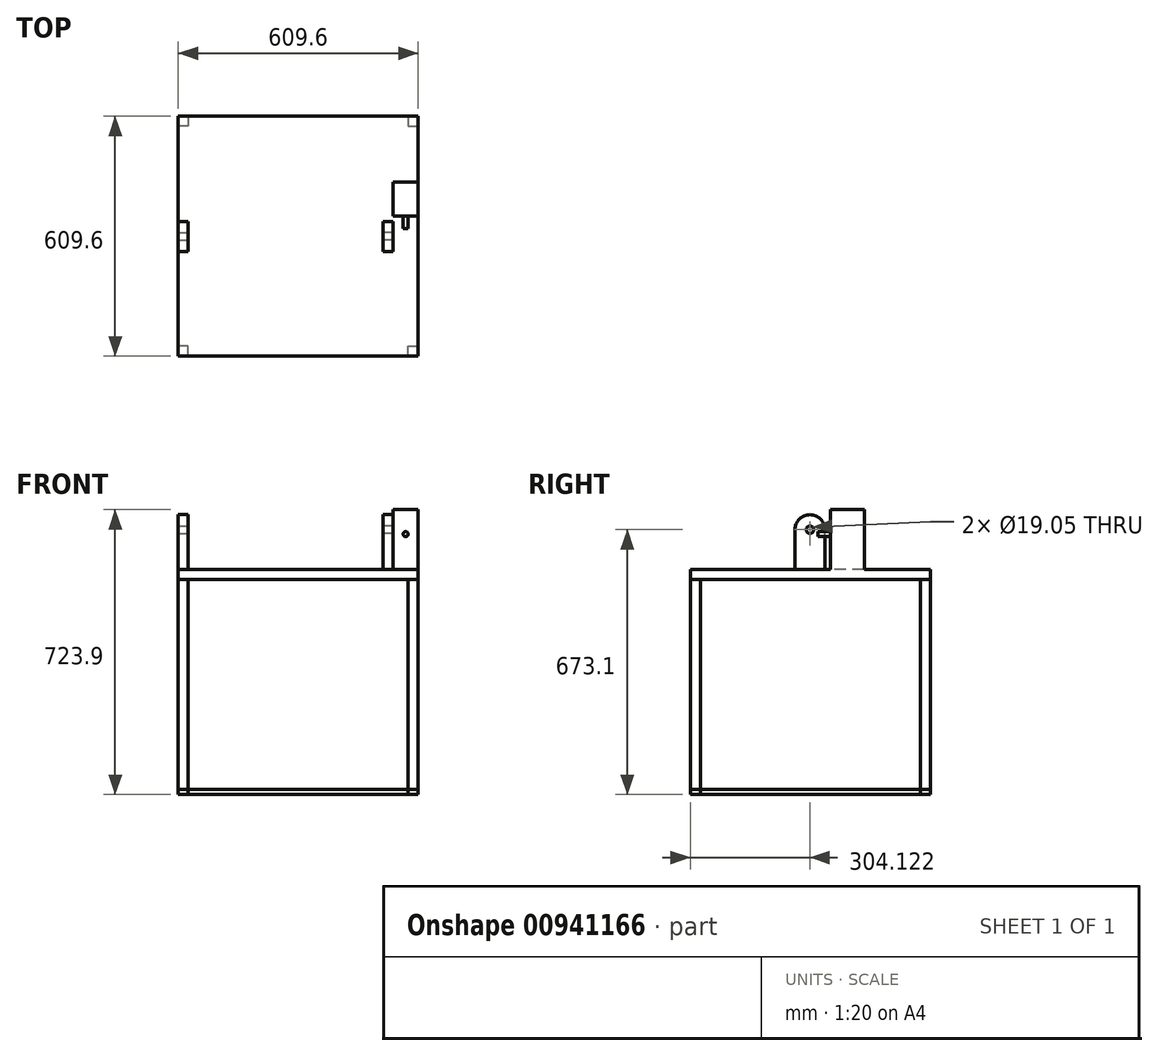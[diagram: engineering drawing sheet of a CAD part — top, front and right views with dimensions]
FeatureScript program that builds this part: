
annotation { "Feature Type Name" : "Feature", "Feature Type Description" : "" }
export const myFeature = defineFeature(function(context is Context, id is Id, definition is map)
    precondition{}
    {
        {
            var Q0;
            Q0=qCreatedBy(makeId("Top.planeOp"),FACE);
            var sketch = newSketch(context, id + "F0", { "sketchPlane" : qUnion([Q0])});
            skLineSegment(sketch, "E0.bottom", {"start": v(-279.4, -304.8) * mm, "end": v(-304.8, -304.8) * mm});
            skLineSegment(sketch, "E0.top", {"start": v(-279.4, -279.4) * mm, "end": v(-304.8, -279.4) * mm});
            skLineSegment(sketch, "E0.left", {"start": v(-279.4, -304.8) * mm, "end": v(-279.4, -279.4) * mm});
            skLineSegment(sketch, "E0.right", {"start": v(-304.8, -304.8) * mm, "end": v(-304.8, -279.4) * mm});
            skPoint(sketch, "E0.middle", {"position": v(-292.1, -292.1) * mm});
            skLineSegment(sketch, "E1.MirrorCS", {"start": v(-279.4, 304.8) * mm, "end": v(-304.8, 304.8) * mm});
            skLineSegment(sketch, "E2.MirrorCS", {"start": v(-279.4, 279.4) * mm, "end": v(-304.8, 279.4) * mm});
            skLineSegment(sketch, "E3.MirrorCS", {"start": v(-304.8, 304.8) * mm, "end": v(-304.8, 279.4) * mm});
            skLineSegment(sketch, "E4.MirrorCS", {"start": v(-279.4, 304.8) * mm, "end": v(-279.4, 279.4) * mm});
            skPoint(sketch, "E5.MirrorP", {"position": v(-292.1, 292.1) * mm});
            skLineSegment(sketch, "E6.MirrorCS", {"start": v(304.8, 304.8) * mm, "end": v(304.8, 279.4) * mm});
            skLineSegment(sketch, "E7.MirrorCS", {"start": v(279.4, 304.8) * mm, "end": v(304.8, 304.8) * mm});
            skLineSegment(sketch, "E8.MirrorCS", {"start": v(279.4, 304.8) * mm, "end": v(279.4, 279.4) * mm});
            skLineSegment(sketch, "E9.MirrorCS", {"start": v(279.4, 279.4) * mm, "end": v(304.8, 279.4) * mm});
            skLineSegment(sketch, "E10.MirrorCS", {"start": v(279.4, -304.8) * mm, "end": v(304.8, -304.8) * mm});
            skLineSegment(sketch, "E11.MirrorCS", {"start": v(279.4, -279.4) * mm, "end": v(304.8, -279.4) * mm});
            skLineSegment(sketch, "E12.MirrorCS", {"start": v(304.8, -304.8) * mm, "end": v(304.8, -279.4) * mm});
            skLineSegment(sketch, "E13.MirrorCS", {"start": v(279.4, -304.8) * mm, "end": v(279.4, -279.4) * mm});
            skPoint(sketch, "E14.MirrorP", {"position": v(292.1, 292.1) * mm});
            skPoint(sketch, "E15.MirrorP", {"position": v(292.1, -292.1) * mm});
            skLineSegment(sketch, "E16.bottom", {"start": v(-215.9, -241.3) * mm, "end": v(-241.3, -241.3) * mm});
            skLineSegment(sketch, "E16.top", {"start": v(-215.9, -215.9) * mm, "end": v(-241.3, -215.9) * mm});
            skLineSegment(sketch, "E16.left", {"start": v(-215.9, -241.3) * mm, "end": v(-215.9, -215.9) * mm});
            skLineSegment(sketch, "E16.right", {"start": v(-241.3, -241.3) * mm, "end": v(-241.3, -215.9) * mm});
            skPoint(sketch, "E16.middle", {"position": v(-228.6, -228.6) * mm});
            skPoint(sketch, "E17.1.0", {"position": v(-228.6, 228.6) * mm});
            skLineSegment(sketch, "E17.1.1", {"start": v(-241.3, 215.9) * mm, "end": v(-241.3, 241.3) * mm});
            skLineSegment(sketch, "E17.1.2", {"start": v(-215.9, 215.9) * mm, "end": v(-215.9, 241.3) * mm});
            skLineSegment(sketch, "E17.1.3", {"start": v(-241.3, 215.9) * mm, "end": v(-215.9, 215.9) * mm});
            skLineSegment(sketch, "E17.1.4", {"start": v(-241.3, 241.3) * mm, "end": v(-215.9, 241.3) * mm});
            skPoint(sketch, "E17.2.0", {"position": v(228.6, 228.6) * mm});
            skLineSegment(sketch, "E17.2.1", {"start": v(215.9, 241.3) * mm, "end": v(241.3, 241.3) * mm});
            skLineSegment(sketch, "E17.2.2", {"start": v(215.9, 215.9) * mm, "end": v(241.3, 215.9) * mm});
            skLineSegment(sketch, "E17.2.3", {"start": v(215.9, 241.3) * mm, "end": v(215.9, 215.9) * mm});
            skLineSegment(sketch, "E17.2.4", {"start": v(241.3, 241.3) * mm, "end": v(241.3, 215.9) * mm});
            skPoint(sketch, "E17.center", {"position": v(0, 0) * mm});
            skLineSegment(sketch, "E17.anchor1", {"start": v(0, 0) * mm, "end": v(-241.3, -241.3) * mm, "construction": true});
            skLineSegment(sketch, "E17.anchor2", {"start": v(0, 0) * mm, "end": v(241.3, -241.3) * mm, "construction": true});
            skLineSegment(sketch, "E18.MirrorCS", {"start": v(241.3, -241.3) * mm, "end": v(241.3, -215.9) * mm});
            skLineSegment(sketch, "E19.MirrorCS", {"start": v(215.9, -215.9) * mm, "end": v(241.3, -215.9) * mm});
            skLineSegment(sketch, "E20.MirrorCS", {"start": v(215.9, -241.3) * mm, "end": v(215.9, -215.9) * mm});
            skLineSegment(sketch, "E21.MirrorCS", {"start": v(215.9, -241.3) * mm, "end": v(241.3, -241.3) * mm});
            skPoint(sketch, "E22.MirrorP", {"position": v(228.6, -228.6) * mm});
            skLineSegment(sketch, "E23.1.3.0", {"start": v(241.3, -215.9) * mm, "end": v(241.3, -241.3) * mm});
            skLineSegment(sketch, "E23.4.3.0", {"start": v(215.9, -215.9) * mm, "end": v(215.9, -241.3) * mm});
            skLineSegment(sketch, "E23.7.3.0", {"start": v(241.3, -215.9) * mm, "end": v(215.9, -215.9) * mm});
            skLineSegment(sketch, "E23.10.3.0", {"start": v(241.3, -241.3) * mm, "end": v(215.9, -241.3) * mm});
            skLineSegment(sketch, "E24", {"start": v(-292.1, 292.1) * mm, "end": v(-228.6, 228.6) * mm});
            skSolve(sketch);
        }
        {
            var Q0;
            Q0=makeQuery(id+"F0.imprint","IMPRINT",FACE,{"disambiguationData":[TD([[makeQuery(id+"F0.imprint","IMPRINT",EDGE,{"derivedFrom":sQuery(id+"F0.wireOp",EDGE,"E3.MirrorCS")}),1.0]])]});
            var Q1;
            Q1=makeQuery(id+"F0.imprint","IMPRINT",FACE,{"disambiguationData":[TD([[makeQuery(id+"F0.imprint","IMPRINT",EDGE,{"derivedFrom":sQuery(id+"F0.wireOp",EDGE,"E6.MirrorCS")}),-1.0]])]});
            var Q2;
            Q2=makeQuery(id+"F0.imprint","IMPRINT",FACE,{"disambiguationData":[TD([[makeQuery(id+"F0.imprint","IMPRINT",EDGE,{"derivedFrom":sQuery(id+"F0.wireOp",EDGE,"E10.MirrorCS")}),1.0]])]});
            var Q3;
            Q3=makeQuery(id+"F0.imprint","IMPRINT",FACE,{"disambiguationData":[TD([[makeQuery(id+"F0.imprint","IMPRINT",EDGE,{"derivedFrom":sQuery(id+"F0.wireOp",EDGE,"E0.bottom")}),-1.0]])]});
            extrude(context, id + "F1", {"entities" : qUnion([Q0, Q1, Q2, Q3]), "depth" : 419.1 * mm, "offsetDistance" : 25.4 * mm, "hasSecondDirection" : true, "secondDirectionOppositeDirection" : true, "secondDirectionDepth" : 127 * mm});
        }
        {
            var Q0;
            Q0=qCreatedBy(makeId("Top.planeOp"),FACE);
            var sketch = newSketch(context, id + "F2", { "sketchPlane" : qUnion([Q0])});
            skLineSegment(sketch, "E25.bottom", {"start": v(304.8, 304.8) * mm, "end": v(-304.8, 304.8) * mm});
            skLineSegment(sketch, "E25.top", {"start": v(304.8, -304.8) * mm, "end": v(-304.8, -304.8) * mm});
            skLineSegment(sketch, "E25.left", {"start": v(304.8, 304.8) * mm, "end": v(304.8, -304.8) * mm});
            skLineSegment(sketch, "E25.right", {"start": v(-304.8, 304.8) * mm, "end": v(-304.8, -304.8) * mm});
            skPoint(sketch, "E25.middle", {"position": v(0, 0) * mm});
            skSolve(sketch);
        }
        {
            var Q0;
            Q0 = qSketchRegion(id + "F2", true);
            extrude(context, id + "F3", {"entities" : qUnion([Q0]), "depth" : 444.5 * mm, "offsetDistance" : 25.4 * mm, "hasSecondDirection" : true, "secondDirectionOppositeDirection" : false, "secondDirectionDepth" : 419.1 * mm});
        }
        {
            var Q0;
            Q0=qCreatedBy(makeId("Right.planeOp"),FACE);
            var sketch = newSketch(context, id + "F4", { "sketchPlane" : qUnion([Q0])});
            skPoint(sketch, "E26", {"position": v(0, 444.5) * mm});
            skLineSegment(sketch, "E27", {"start": v(-38.78, 444.5) * mm, "end": v(37.42, 444.5) * mm});
            skLineSegment(sketch, "E28", {"start": v(37.42, 444.5) * mm, "end": v(37.42, 546.1) * mm});
            skLineSegment(sketch, "E29", {"start": v(-38.78, 444.5) * mm, "end": v(-38.78, 546.1) * mm});
            skArc(sketch, "E30", {"start": v(37.42, 546.1) * mm, "mid": v(-0.68, 584.2) * mm, "end": v(-38.78, 546.1) * mm});
            skCircle(sketch, "E31", {"center": v(-0.68, 546.1) * mm, "radius": 9.53 * mm});
            skSolve(sketch);
        }
        {
            var Q0;
            Q0=makeQuery(id+"F4.imprint","IMPRINT",FACE,{"disambiguationData":[TD([[makeQuery(id+"F4.imprint","IMPRINT",EDGE,{"derivedFrom":sQuery(id+"F4.wireOp",EDGE,"E27")}),1.0]])]});
            extrude(context, id + "F5", {"entities" : qUnion([Q0]), "operationType" : NewBodyOperationType.ADD, "depth" : -304.8 * mm, "offsetDistance" : 25.4 * mm, "hasSecondDirection" : true, "secondDirectionOppositeDirection" : true, "secondDirectionDepth" : 279.4 * mm});
        }
        {
            var Q0;
            Q0 = qSketchRegion(id + "F4", true);
            extrude(context, id + "F6", {"entities" : qUnion([Q0]), "operationType" : NewBodyOperationType.ADD, "oppositeDirection" : true, "depth" : -241.3 * mm, "offsetDistance" : 25.4 * mm, "hasSecondDirection" : true, "secondDirectionOppositeDirection" : false, "secondDirectionDepth" : 215.9 * mm});
        }
        {
            var Q0;
            Q0=makeQuery(id+"F3.opExtrude","CAP_FACE",FACE,{"disambiguationData":[OSD([sQuery(id+"F2.wireOp",EDGE,"E25.bottom"),sQuery(id+"F2.wireOp",EDGE,"E25.top"),sQuery(id+"F2.wireOp",EDGE,"E25.left"),sQuery(id+"F2.wireOp",EDGE,"E25.right")])],"isStart":false});
            var sketch = newSketch(context, id + "F7", { "sketchPlane" : qUnion([Q0])});
            skLineSegment(sketch, "E32.bottom", {"start": v(304.8, 137.1) * mm, "end": v(241.3, 137.1) * mm});
            skLineSegment(sketch, "E32.top", {"start": v(304.8, 50.8) * mm, "end": v(241.3, 50.8) * mm});
            skLineSegment(sketch, "E32.left", {"start": v(304.8, 137.1) * mm, "end": v(304.8, 50.8) * mm});
            skLineSegment(sketch, "E32.right", {"start": v(241.3, 137.1) * mm, "end": v(241.3, 50.8) * mm});
            skSolve(sketch);
        }
        {
            var Q0;
            Q0=makeQuery(id+"F7.imprint","IMPRINT",FACE,{"disambiguationData":[TD([[makeQuery(id+"F7.imprint","IMPRINT",EDGE,{"derivedFrom":sQuery(id+"F7.wireOp",EDGE,"E32.bottom")}),1.0]])]});
            extrude(context, id + "F8", {"entities" : qUnion([Q0]), "operationType" : NewBodyOperationType.ADD, "depth" : 152.4 * mm, "offsetDistance" : 25.4 * mm});
        }
        {
            var Q0;
            Q0=makeQuery(id+"F8.opExtrude","SWEPT_FACE",FACE,{"disambiguationData":[OSD([sQuery(id+"F7.wireOp",EDGE,"E32.top")])]});
            var sketch = newSketch(context, id + "F9", { "sketchPlane" : qUnion([Q0])});
            skCircle(sketch, "E33", {"center": v(273.05, 534.8) * mm, "radius": 6.35 * mm});
            skSolve(sketch);
        }
        {
            var Q0;
            Q0 = qSketchRegion(id + "F9", true);
            extrude(context, id + "F10", {"entities" : qUnion([Q0]), "operationType" : NewBodyOperationType.ADD, "depth" : 31.75 * mm, "offsetDistance" : 25.4 * mm});
        }
        {
            var Q0;
            Q0=qCreatedBy(makeId("Top.planeOp"),FACE);
            var sketch = newSketch(context, id + "F11", { "sketchPlane" : qUnion([Q0])});
            skLineSegment(sketch, "E34.bottom", {"start": v(304.8, 304.8) * mm, "end": v(-304.8, 304.8) * mm});
            skLineSegment(sketch, "E34.top", {"start": v(304.8, -304.8) * mm, "end": v(-304.8, -304.8) * mm});
            skLineSegment(sketch, "E34.left", {"start": v(304.8, 304.8) * mm, "end": v(304.8, -304.8) * mm});
            skLineSegment(sketch, "E34.right", {"start": v(-304.8, 304.8) * mm, "end": v(-304.8, -304.8) * mm});
            skPoint(sketch, "E34.middle", {"position": v(0, 0) * mm});
            skSolve(sketch);
        }
        {
            var Q0;
            {var subQ2=sQuery(id+"F11.wireOp",EDGE,"E34.top");Q0=makeQuery(id+"F11.imprint","IMPRINT",FACE,{"disambiguationData":[TD([[makeQuery(id+"F11.imprint","IMPRINT",EDGE,{"derivedFrom":subQ2}),-1.0]])]});}
            extrude(context, id + "F12", {"entities" : qUnion([Q0]), "oppositeDirection" : true, "depth" : 127 * mm, "offsetDistance" : 25.4 * mm, "hasSecondDirection" : true, "secondDirectionOppositeDirection" : true, "secondDirectionDepth" : 114.3 * mm});
        }
    });
